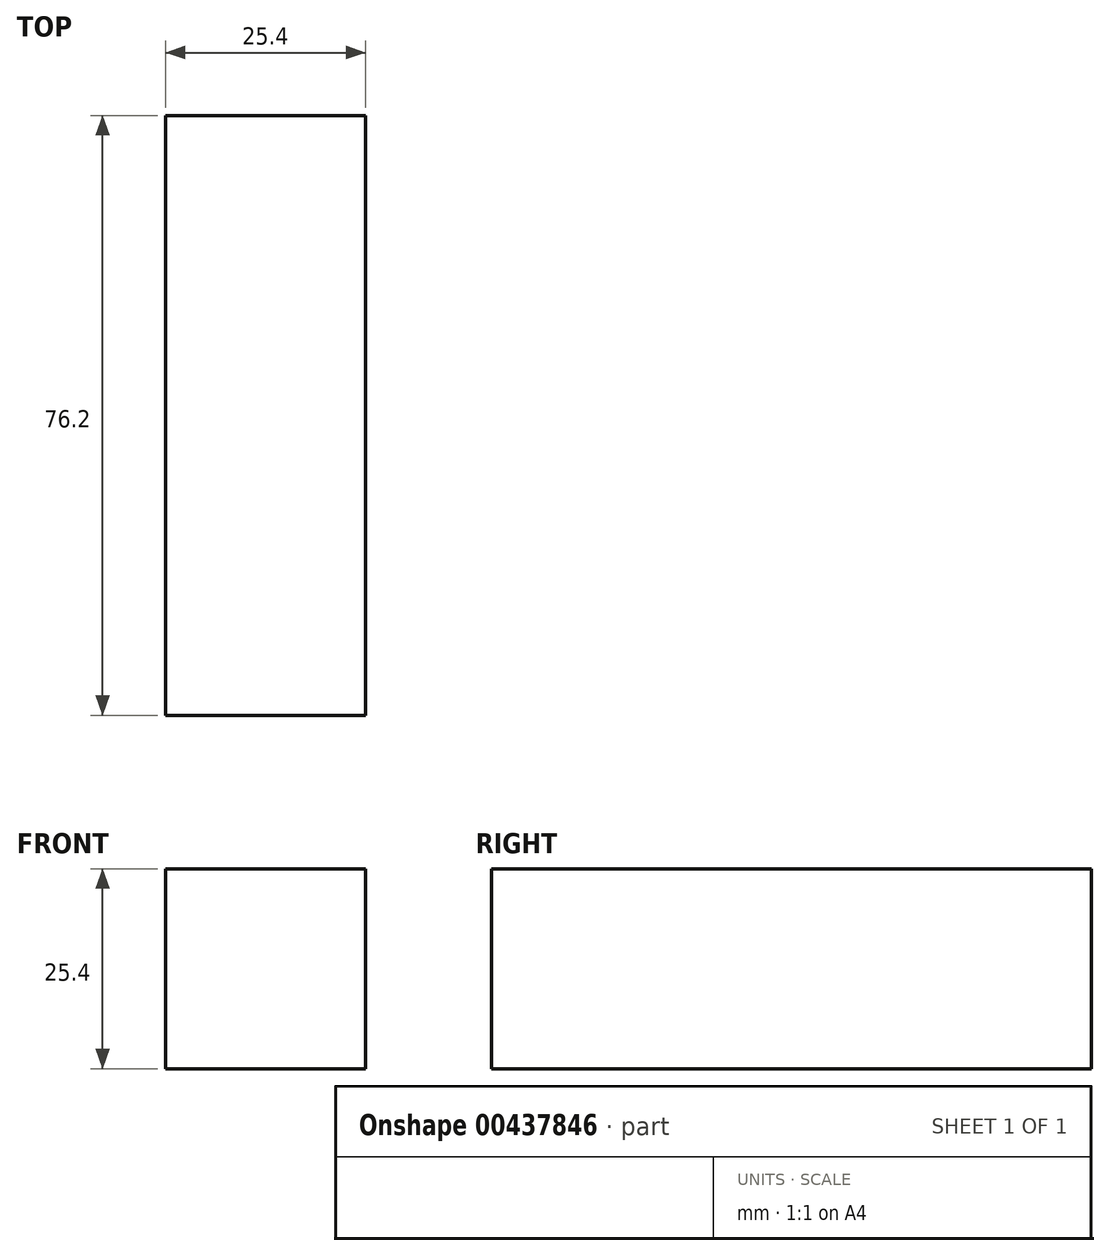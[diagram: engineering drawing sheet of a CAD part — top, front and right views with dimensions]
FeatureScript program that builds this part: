
annotation { "Feature Type Name" : "Feature", "Feature Type Description" : "" }
export const myFeature = defineFeature(function(context is Context, id is Id, definition is map)
    precondition{}
    {
        {
            var Q0;
            Q0=qCreatedBy(makeId("Front.planeOp"),FACE);
            var sketch = newSketch(context, id + "F0", { "sketchPlane" : qUnion([Q0])});
            skLineSegment(sketch, "E0.bottom", {"start": v(-66.07, 56.72) * mm, "end": v(-40.67, 56.72) * mm});
            skLineSegment(sketch, "E0.top", {"start": v(-66.07, 31.32) * mm, "end": v(-40.67, 31.32) * mm});
            skLineSegment(sketch, "E0.left", {"start": v(-66.07, 56.72) * mm, "end": v(-66.07, 31.32) * mm});
            skLineSegment(sketch, "E0.right", {"start": v(-40.67, 56.72) * mm, "end": v(-40.67, 31.32) * mm});
            skSolve(sketch);
        }
        {
            var Q0;
            Q0 = qSketchRegion(id + "F0", true);
            extrude(context, id + "F1", {"entities" : qUnion([Q0]), "depth" : 76.2 * mm});
        }
    });
